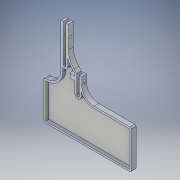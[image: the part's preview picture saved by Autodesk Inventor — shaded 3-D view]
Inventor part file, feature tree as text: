
AUTODESK INVENTOR PART (.ipt)
format: ipt  version: 2017 (Build 210142000, 142)  size: 266,240 bytes
history: native  units: in
note: dims shown in document units (in); Inventor stores cm internally (conversion verified against a paired STEP export)
features: sketch x15, extrude x12, fillet x5, shell x1
ambient origin geometry x8: Origin, YZ Plane, XZ Plane, XY Plane, X Axis, Y Axis, Z Axis, Center Point
bodies: Solid1 (feature_tree)
feature tree (33):
  extrude  "Extrusion1"  Depth=2.0in
  sketch  "Sketch2"  dims[d3=4.5in d4=0.125in d5=0.0in]
  extrude  "Extrusion2"  Depth=0.125in TaperAngle=0.0deg
  extrude  "Extrusion3"  Depth=0.066in
  extrude  "Extrusion4"  Depth=0.25in
  extrude  "Extrusion5"  Depth=0.125in TaperAngle=0.0deg
  extrude  "Extrusion6"  Depth=3.0in TaperAngle=0.0deg
  sketch  "Sketch6"  dims[d14=3.0in d15=0.0in d16=3.0in d17=0.0in]
  sketch  "Sketch7"  dims[d18=0.75in d19=0.125in]
  sketch  "Sketch8"  dims[d20=2.0in d21=0.0in d22=1.64in]
  sketch  "Sketch9"  dims[d23=0.125in d24=2.0in d25=0.0in]
  extrude  "Extrusion11"  Depth=0.125in
  extrude  "Extrusion12"  Depth=2.0in
  extrude  "Extrusion13"  Depth=2.0in TaperAngle=0.0deg
  extrude  "Extrusion14"  Depth=0.125in
  extrude  "Extrusion15"  Depth=0.125in
  extrude  "Extrusion16"  Depth=0.125in
  fillet  "Fillet1"  Radius=0.25in
  fillet  "Fillet3"  Radius=0.067in
  fillet  "Fillet4"  Radius=0.125in
  fillet  "Fillet5"  Radius=0.25in
  fillet  "Fillet6"  Radius=0.125in
  shell  "Shell1"  Thickness=0.25in
  sketch  "Sketch1"  dims[d1=4.5in d2=2.0in]
  sketch  "Sketch3"  dims[d7=0.066in d8=0.066in]
  sketch  "Sketch4"  dims[d9=0.125in d10=0.25in]
  sketch  "Sketch5"  dims[d11=0.125in d12=0.125in d13=0.0in]
  sketch  "Sketch12"  dims[d30=0.125in d34=0.125in]
  sketch  "Sketch13"  dims[d35=0.132in d36=0.125in]
  sketch  "Sketch14"  dims[d44=0.067in d45=0.125in d46=0.25in d47=0.0in d48=0.067in d49=0.125in d50=0.25in d51=0.0in d52=0.125in d55=0.25in d56=0.0in]
  sketch  "Sketch15"  dims[d57=2.0in d58=0.0in]
  sketch  "Sketch16"  dims[d59=0.25in d60=0.0in]
  sketch  "Sketch17"  dims[d61=0.5in d62=0.0in d63=0.0625in d65=1.0in d67=0.625in d68=0.0625in d69=0.75in d70=0.1in]
